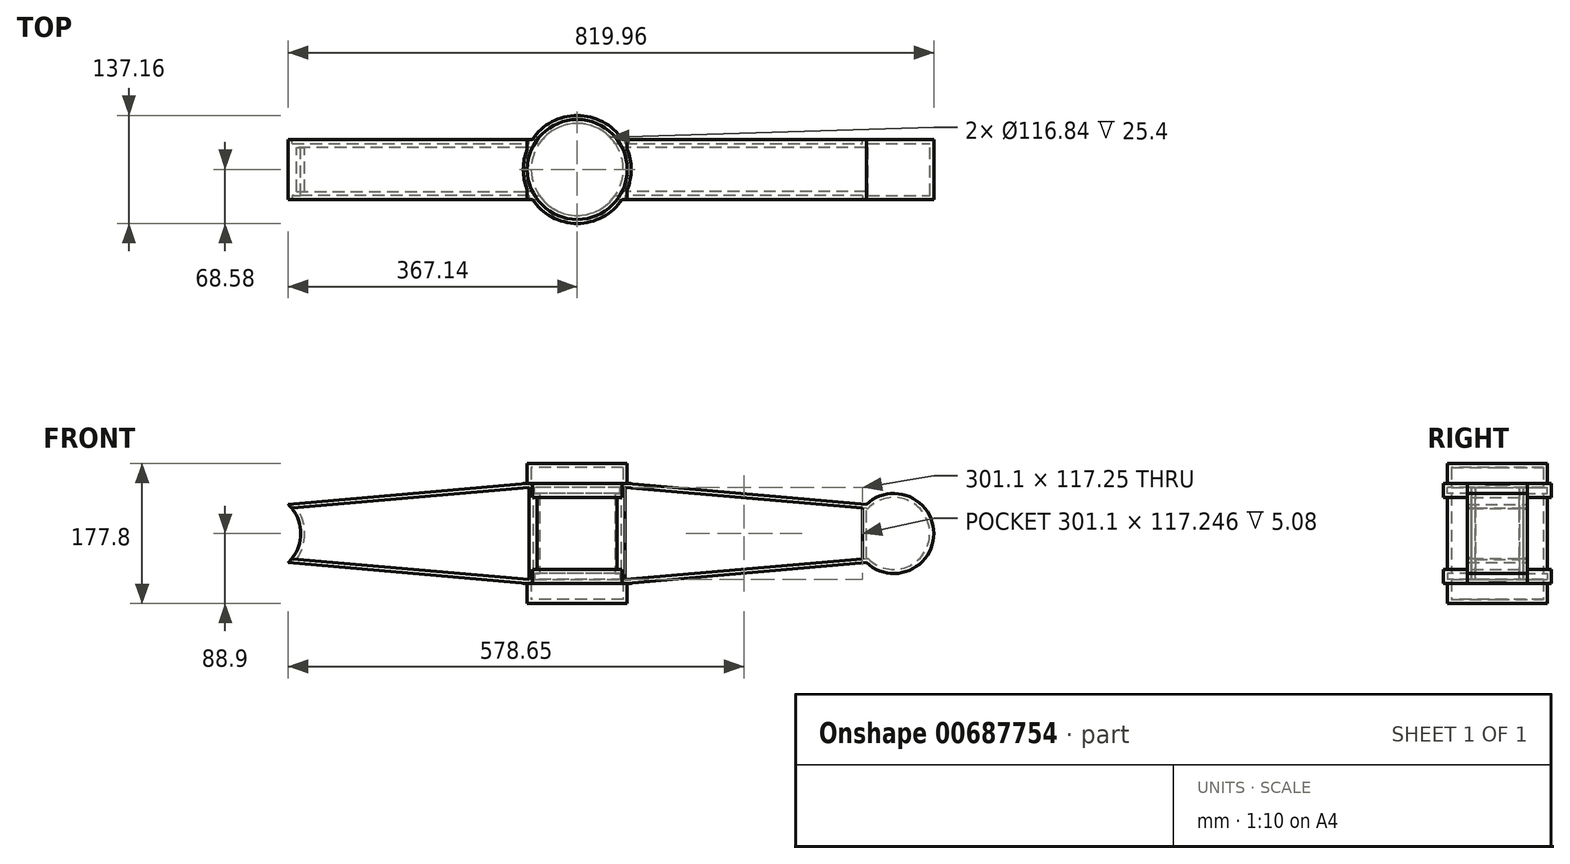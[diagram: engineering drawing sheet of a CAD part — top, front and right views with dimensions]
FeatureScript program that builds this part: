
annotation { "Feature Type Name" : "Feature", "Feature Type Description" : "" }
export const myFeature = defineFeature(function(context is Context, id is Id, definition is map)
    precondition{}
    {
        {
            var Q0;
            Q0=qCreatedBy(makeId("Top.planeOp"),FACE);
            var sketch = newSketch(context, id + "F0", { "sketchPlane" : qUnion([Q0])});
            skCircle(sketch, "E0", {"center": v(0, 0) * mm, "radius": 63.5 * mm});
            skSolve(sketch);
        }
        {
            var Q0;
            Q0 = qSketchRegion(id + "F0", true);
            var Q1;
            Q1=makeQuery(id+"F0.imprint","IMPRINT",FACE,{"disambiguationData":[TD([[makeQuery(id+"F0.imprint","IMPRINT",EDGE,{"derivedFrom":sQuery(id+"F0.wireOp",EDGE,"E0")}),1.0]])]});
            extrude(context, id + "F1", {"entities" : qUnion([Q0, Q1]), "depth" : 177.8 * mm, "offsetDistance" : 25.4 * mm});
        }
        {
            var Q0;
            Q0=qCreatedBy(makeId("Top.planeOp"),FACE);
            cPlane(context, id + "F2", {"entities" : qUnion([Q0]), "cplaneType" : CPlaneType.OFFSET, "offset" : 25.4 * mm, "width" : 152.4 * mm, "height" : 152.4 * mm});
        }
        {
            var Q0;
            Q0=qCreatedBy(id+"F2.planeOp",FACE);
            var sketch = newSketch(context, id + "F3", { "sketchPlane" : qUnion([Q0])});
            skCircle(sketch, "E1", {"center": v(0, 0) * mm, "radius": 68.58 * mm});
            skSolve(sketch);
        }
        {
            var Q0;
            Q0=makeQuery(id+"F3.imprint","IMPRINT",FACE,{"disambiguationData":[TD([[makeQuery(id+"F3.imprint","IMPRINT",EDGE,{"derivedFrom":sQuery(id+"F3.wireOp",EDGE,"E1")}),1.0]])]});
            extrude(context, id + "F4", {"entities" : qUnion([Q0]), "operationType" : NewBodyOperationType.ADD, "depth" : 17.78 * mm, "offsetDistance" : 25.4 * mm});
        }
        {
            var Q0;
            Q0=makeQuery(id+"F1.opExtrude","CAP_FACE",FACE,{"disambiguationData":[OSD([sQuery(id+"F0.wireOp",EDGE,"E0")])],"isStart":false});
            cPlane(context, id + "F5", {"entities" : qUnion([Q0]), "cplaneType" : CPlaneType.OFFSET, "offset" : 25.4 * mm, "oppositeDirection" : true, "width" : 152.4 * mm, "height" : 152.4 * mm});
        }
        {
            var Q0;
            Q0=qCreatedBy(id+"F5.planeOp",FACE);
            var sketch = newSketch(context, id + "F6", { "sketchPlane" : qUnion([Q0])});
            skCircle(sketch, "E2", {"center": v(0, 0) * mm, "radius": 68.58 * mm});
            skSolve(sketch);
        }
        {
            var Q0;
            Q0=makeQuery(id+"F6.imprint","IMPRINT",FACE,{"disambiguationData":[TD([[makeQuery(id+"F6.imprint","IMPRINT",EDGE,{"derivedFrom":sQuery(id+"F6.wireOp",EDGE,"E2")}),1.0]])]});
            extrude(context, id + "F7", {"entities" : qUnion([Q0]), "operationType" : NewBodyOperationType.ADD, "oppositeDirection" : true, "depth" : 17.78 * mm, "offsetDistance" : 25.4 * mm});
        }
        {
            var Q0;
            Q0=qCreatedBy(makeId("Front.planeOp"),FACE);
            var sketch = newSketch(context, id + "F8", { "sketchPlane" : qUnion([Q0])});
            skLineSegment(sketch, "E3", {"start": v(63.5, 152.4) * mm, "end": v(367.14, 125.83) * mm});
            skLineSegment(sketch, "E4", {"start": v(63.5, 25.4) * mm, "end": v(367.14, 51.97) * mm});
            skLineSegment(sketch, "E5", {"start": v(63.5, 177.8) * mm, "end": v(63.5, 152.4) * mm});
            skLineSegment(sketch, "E6", {"start": v(68.58, 152.4) * mm, "end": v(68.58, 134.62) * mm});
            skLineSegment(sketch, "E7", {"start": v(-68.58, 134.62) * mm, "end": v(-68.58, 152.4) * mm});
            skLineSegment(sketch, "E8", {"start": v(63.5, 25.4) * mm, "end": v(63.5, 0) * mm});
            skLineSegment(sketch, "E9", {"start": v(-68.58, 25.4) * mm, "end": v(-68.58, 43.18) * mm});
            skLineSegment(sketch, "E10", {"start": v(68.58, 43.18) * mm, "end": v(68.58, 25.4) * mm});
            skCircle(sketch, "E11", {"center": v(402.02, 88.9) * mm, "radius": 50.8 * mm});
            skLineSegment(sketch, "E12", {"start": v(0, -57.94) * mm, "end": v(0, 226.5) * mm});
            skLineSegment(sketch, "E13.MirrorCS", {"start": v(-63.5, 152.4) * mm, "end": v(-367.14, 125.83) * mm});
            skLineSegment(sketch, "E14.MirrorCS", {"start": v(-63.5, 25.4) * mm, "end": v(-367.14, 51.97) * mm});
            skCircle(sketch, "E15.MirrorC", {"center": v(-402.02, 88.9) * mm, "radius": 50.8 * mm});
            skLineSegment(sketch, "E16", {"start": v(-63.5, 152.4) * mm, "end": v(-48.26, 152.4) * mm});
            skLineSegment(sketch, "E17", {"start": v(-48.26, 152.4) * mm, "end": v(-48.26, 25.4) * mm});
            skLineSegment(sketch, "E18", {"start": v(-48.26, 25.4) * mm, "end": v(-63.5, 25.4) * mm});
            skLineSegment(sketch, "E19", {"start": v(63.5, 152.4) * mm, "end": v(48.26, 152.4) * mm});
            skLineSegment(sketch, "E20", {"start": v(48.26, 152.4) * mm, "end": v(48.26, 25.4) * mm});
            skLineSegment(sketch, "E21", {"start": v(48.26, 25.4) * mm, "end": v(68.58, 25.4) * mm});
            skSolve(sketch);
        }
        {
            var Q0;
            {var subQ4=sQuery(id+"F8.wireOp",EDGE,"fjsv5gT4-ox5l-RbgW-5QOI-JZ3Mzcbwu0NB");Q0=makeQuery(id+"F8.imprint","IMPRINT",FACE,{"disambiguationData":[TD([[makeQuery(id+"F8.imprint","IMPRINT",EDGE,{"derivedFrom":subQ4}),1.0]])]});}
            var Q1;
            {var subQ4=sQuery(id+"F8.wireOp",EDGE,"VerUzKcr-cCtI-6mlB-pRHj-EzGH7lbOn3qb");Q1=makeQuery(id+"F8.imprint","IMPRINT",FACE,{"disambiguationData":[TD([[makeQuery(id+"F8.imprint","IMPRINT",EDGE,{"derivedFrom":subQ4}),1.0]])]});}
            var Q2;
            {var subQ0=sQuery(id+"F8.wireOp",EDGE,"E15.MirrorC");var subQ1=makeQuery(id+"F8.imprint","INTERSECT",VERTEX,{"derivedFrom":[sQuery(id+"F8.wireOp",EDGE,"E13.MirrorCS"),subQ0]});Q2=makeQuery(id+"F8.imprint","IMPRINT",FACE,{"disambiguationData":[TD([[makeQuery(id+"F8.imprint","IMPRINT",EDGE,{"disambiguationData":[TD([[subQ1,-1.0]])],"derivedFrom":subQ0}),-1.0]])]});}
            var Q3;
            {var subQ0=sQuery(id+"F8.wireOp",EDGE,"E11");var subQ1=makeQuery(id+"F8.imprint","INTERSECT",VERTEX,{"derivedFrom":[sQuery(id+"F8.wireOp",EDGE,"E3"),subQ0]});Q3=makeQuery(id+"F8.imprint","IMPRINT",FACE,{"disambiguationData":[TD([[makeQuery(id+"F8.imprint","IMPRINT",EDGE,{"disambiguationData":[TD([[subQ1,-1.0]])],"derivedFrom":subQ0}),1.0]])]});}
            var Q4;
            {var subQ8=sQuery(id+"F8.wireOp",EDGE,"E16");Q4=makeQuery(id+"F8.imprint","IMPRINT",FACE,{"disambiguationData":[TD([[makeQuery(id+"F8.imprint","IMPRINT",EDGE,{"derivedFrom":subQ8}),-1.0]])]});}
            var Q5;
            {var subQ9=sQuery(id+"F8.wireOp",EDGE,"E19");Q5=makeQuery(id+"F8.imprint","IMPRINT",FACE,{"disambiguationData":[TD([[makeQuery(id+"F8.imprint","IMPRINT",EDGE,{"derivedFrom":subQ9}),1.0]])]});}
            extrude(context, id + "F9", {"entities" : qUnion([Q0, Q1, Q2, Q3, Q4, Q5]), "operationType" : NewBodyOperationType.ADD, "endBound" : BoundingType.SYMMETRIC, "depth" : 76.2 * mm, "offsetDistance" : 25.4 * mm});
        }
        {
            var Q0;
            Q0=makeQuery(id+"F9.opExtrude","CAP_FACE",FACE,{"disambiguationData":[OSD([sQuery(id+"F8.wireOp",EDGE,"E13.MirrorCS"),sQuery(id+"F8.wireOp",EDGE,"E14.MirrorCS"),sQuery(id+"F8.wireOp",EDGE,"E15.MirrorC"),sQuery(id+"F8.wireOp",EDGE,"E16"),sQuery(id+"F8.wireOp",EDGE,"E17"),sQuery(id+"F8.wireOp",EDGE,"E18")])],"isStart":false});
            var sketch = newSketch(context, id + "F10", { "sketchPlane" : qUnion([Q0])});
            skLineSegment(sketch, "E22", {"start": v(-60.96, 147.52) * mm, "end": v(-60.96, 30.28) * mm});
            skLineSegment(sketch, "E23", {"start": v(-60.96, 30.28) * mm, "end": v(-362.06, 56.62) * mm});
            skLineSegment(sketch, "E24", {"start": v(-362.06, 56.62) * mm, "end": v(-362.06, 121.18) * mm});
            skLineSegment(sketch, "E25", {"start": v(-362.06, 121.18) * mm, "end": v(-60.96, 147.52) * mm});
            skLineSegment(sketch, "E26", {"start": v(0, -49.07) * mm, "end": v(0, 228.68) * mm});
            skLineSegment(sketch, "E27.MirrorCS", {"start": v(60.96, 147.52) * mm, "end": v(60.96, 30.28) * mm});
            skLineSegment(sketch, "E28.MirrorCS", {"start": v(362.06, 121.18) * mm, "end": v(60.96, 147.52) * mm});
            skLineSegment(sketch, "E29.MirrorCS", {"start": v(60.96, 30.28) * mm, "end": v(362.06, 56.62) * mm});
            skLineSegment(sketch, "E30.MirrorCS", {"start": v(362.06, 56.62) * mm, "end": v(362.06, 121.18) * mm});
            skSolve(sketch);
        }
        {
            var Q0;
            Q0=makeQuery(id+"F9.opExtrude","CAP_FACE",FACE,{"disambiguationData":[OSD([sQuery(id+"F8.wireOp",EDGE,"E3"),sQuery(id+"F8.wireOp",EDGE,"E4"),sQuery(id+"F8.wireOp",EDGE,"E11"),sQuery(id+"F8.wireOp",EDGE,"E19"),sQuery(id+"F8.wireOp",EDGE,"E20"),sQuery(id+"F8.wireOp",EDGE,"E21")])],"isStart":true});
            var sketch = newSketch(context, id + "F11", { "sketchPlane" : qUnion([Q0])});
            skLineSegment(sketch, "E31.0", {"start": v(-362.06, 56.62) * mm, "end": v(-362.06, 121.18) * mm});
            skLineSegment(sketch, "E32.0", {"start": v(-362.06, 121.18) * mm, "end": v(-60.96, 147.52) * mm});
            skLineSegment(sketch, "E33.0", {"start": v(-60.96, 30.28) * mm, "end": v(-362.06, 56.62) * mm});
            skLineSegment(sketch, "E34.0", {"start": v(-60.96, 147.52) * mm, "end": v(-60.96, 30.28) * mm});
            skLineSegment(sketch, "E35.0", {"start": v(60.96, 147.52) * mm, "end": v(60.96, 30.28) * mm});
            skLineSegment(sketch, "E36.0", {"start": v(362.06, 121.18) * mm, "end": v(60.96, 147.52) * mm});
            skLineSegment(sketch, "E37.0", {"start": v(60.96, 30.28) * mm, "end": v(362.06, 56.62) * mm});
            skLineSegment(sketch, "E38.0", {"start": v(362.06, 56.62) * mm, "end": v(362.06, 121.18) * mm});
            skSolve(sketch);
        }
        {
            var Q0;
            Q0=makeQuery(id+"F11.imprint","IMPRINT",FACE,{"disambiguationData":[TD([[makeQuery(id+"F11.imprint","IMPRINT",EDGE,{"derivedFrom":sQuery(id+"F11.wireOp",EDGE,"E35.0")}),1.0]])]});
            var Q1;
            Q1=makeQuery(id+"F11.imprint","IMPRINT",FACE,{"disambiguationData":[TD([[makeQuery(id+"F11.imprint","IMPRINT",EDGE,{"derivedFrom":sQuery(id+"F11.wireOp",EDGE,"E31.0")}),-1.0]])]});
            extrude(context, id + "F12", {"entities" : qUnion([Q0, Q1]), "operationType" : NewBodyOperationType.REMOVE, "oppositeDirection" : true, "depth" : 5.08 * mm, "offsetDistance" : 25.4 * mm});
        }
        {
            var Q0;
            Q0=makeQuery(id+"F10.imprint","IMPRINT",FACE,{"disambiguationData":[TD([[makeQuery(id+"F10.imprint","IMPRINT",EDGE,{"derivedFrom":sQuery(id+"F10.wireOp",EDGE,"E22")}),-1.0]])]});
            var Q1;
            Q1=makeQuery(id+"F10.imprint","IMPRINT",FACE,{"disambiguationData":[TD([[makeQuery(id+"F10.imprint","IMPRINT",EDGE,{"derivedFrom":sQuery(id+"F10.wireOp",EDGE,"E27.MirrorCS")}),1.0]])]});
            extrude(context, id + "F13", {"entities" : qUnion([Q0, Q1]), "operationType" : NewBodyOperationType.REMOVE, "oppositeDirection" : true, "depth" : 5.08 * mm, "offsetDistance" : 25.4 * mm});
        }
        {
            var Q0;
            Q0=makeQuery(id+"F12.boolean.opBoolean","COPY",FACE,{"derivedFrom":makeQuery(id+"F12.opExtrude","CAP_FACE",FACE,{"disambiguationData":[OSD([sQuery(id+"F11.wireOp",EDGE,"E31.0"),sQuery(id+"F11.wireOp",EDGE,"E32.0"),sQuery(id+"F11.wireOp",EDGE,"E33.0"),sQuery(id+"F11.wireOp",EDGE,"E34.0")])],"isStart":false})});
            var Q1;
            Q1=makeQuery(id+"F12.boolean.opBoolean","COPY",FACE,{"derivedFrom":makeQuery(id+"F12.opExtrude","CAP_FACE",FACE,{"disambiguationData":[OSD([sQuery(id+"F11.wireOp",EDGE,"E35.0"),sQuery(id+"F11.wireOp",EDGE,"E36.0"),sQuery(id+"F11.wireOp",EDGE,"E37.0"),sQuery(id+"F11.wireOp",EDGE,"E38.0")])],"isStart":false})});
            var Q2;
            Q2=makeQuery(id+"F1.opExtrude","SWEPT_BODY",BODY,{"disambiguationData":[OSD([sQuery(id+"F0.wireOp",EDGE,"E0")])]});
            shell(context, id + "F14", {"isHollow" : true, "entities" : qUnion([Q0, Q1]), "parts" : qUnion([Q2]), "thickness" : 5.08 * mm});
        }
    });
